# Revit family: СЗ-ВО
name_source: partatom
category: Арматура воздуховодов
units: mm (PartAtom-declared; Revit-internal decimal feet)

## family parameters
Всегда вертикально = Да
На основе рабочей плоскости = Нет
Общий = Нет
При загрузке вырезать с полостями = Нет
Размер круглого соединителя = Использовать диаметр
Тип детали = Присоединяется

## types (11) — shared parameters
00_20_Manufacturer = Вентс
00_20_Name = Захисна сітка
Casing Material = Условный материал-отделка
Load Classification = HVAC
Maintenance zone material = <По категории>
zero-valued in all types: Отметка по умолчанию

## per-type parameters (varying)
| type | D1 | D2 | Dy | Grid Material | R1 | d | n | Вес |
| СЗ-ВО-400 | 450 мм | 490 мм | 400 мм | Сетка, сталь, окрашенная, RAL5007 | 225 мм | 8 мм | 12 | 1.28 кг |
| СЗ-ВО-450 | 500 мм | 540 мм | 450 мм | Cover Grid Cross | 250 мм | 8 мм | 12 | 1.45 кг |
| СЗ-ВО-500 | 560 мм | 600 мм | 500 мм | Cover Grid Cross | 280 мм | 12 мм | 12 | 1.77 кг |
| СЗ-ВО-560 | 620 мм | 660 мм | 560 мм | Cover Grid Cross | 310 мм | 12 мм | 12 | 2 кг |
| СЗ-ВО-630 | 690 мм | 730 мм | 630 мм | Cover Grid Cross | 345 мм | 12 мм | 12 | 2.28 кг |
| СЗ-ВО-710 | 770 мм | 810 мм | 710 мм | Cover Grid Cross | 385 мм | 12 мм | 16 | 2.28 кг |
| СЗ-ВО-800 | 860 мм | 900 мм | 800 мм | Cover Grid Cross | 430 мм | 12 мм | 16 | 2.59 кг |
| СЗ-ВО-900 | 970 мм | 1015 мм | 900 мм | Сетка, сталь, окрашенная, RAL5007 | 485 мм | 15 мм | 16 | 3.83 кг |
| СЗ-ВО-1000 | 1070 мм | 1115 мм | 1000 мм | Cover Grid Cross | 535 мм | 15 мм | 16 | 4.32 кг |
| СЗ-ВО-1120 | 1190 мм | 1270 мм | 1120 мм | Cover Grid Cross | 595 мм | 15 мм | 20 | 6.2 кг |
| СЗ-ВО-1250 | 1320 мм | 1400 мм | 1250 мм | Сетка, сталь, окрашенная, RAL5007 | 660 мм | 15 мм | 20 | 7.03 кг |

note: column(s) folded — value = type name in every type: 00_20_Type
